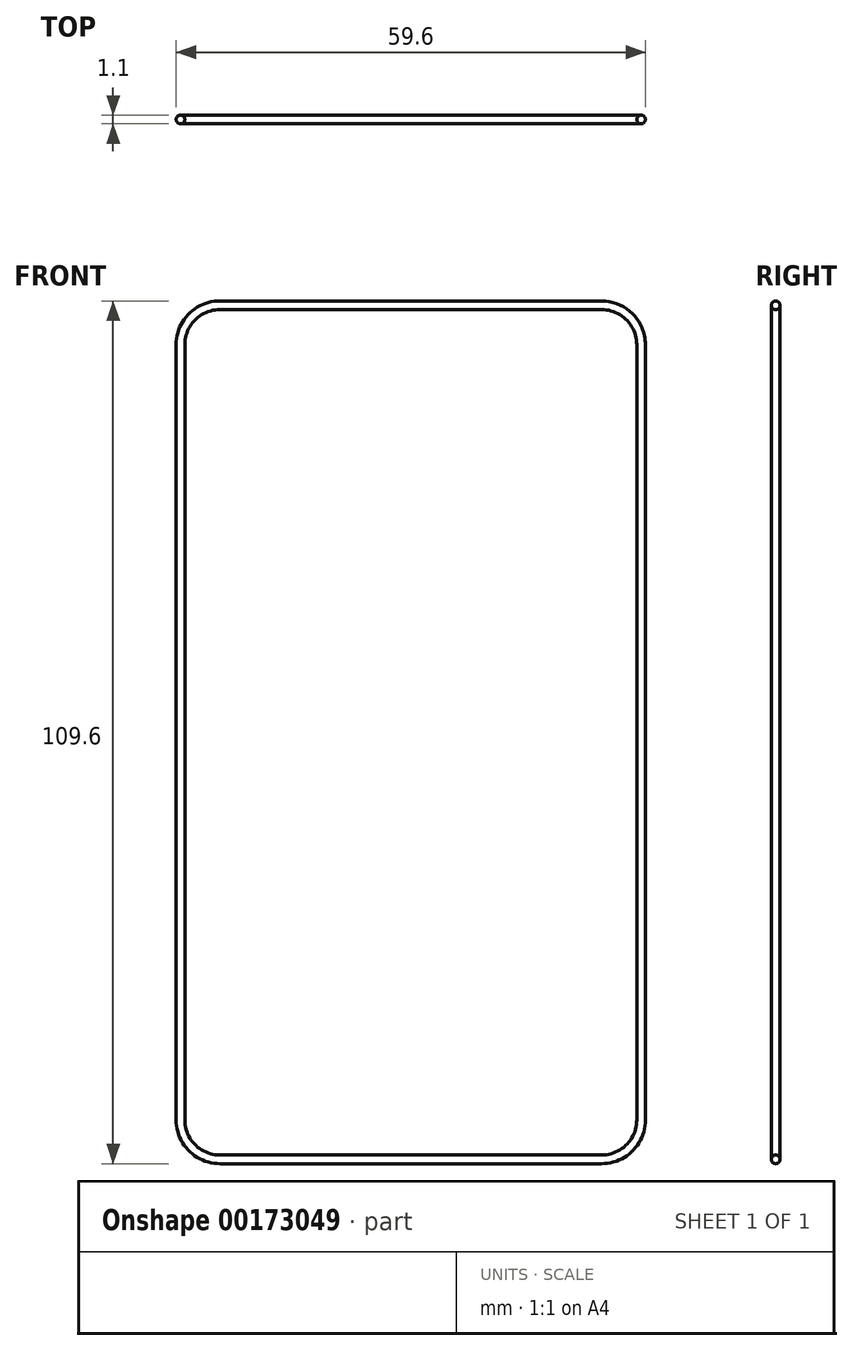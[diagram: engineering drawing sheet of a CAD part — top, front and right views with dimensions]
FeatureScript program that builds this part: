
annotation { "Feature Type Name" : "Feature", "Feature Type Description" : "" }
export const myFeature = defineFeature(function(context is Context, id is Id, definition is map)
    precondition{}
    {
        {
            var Q0;
            Q0=qCreatedBy(makeId("Front.planeOp"),FACE);
            var sketch = newSketch(context, id + "F0", { "sketchPlane" : qUnion([Q0])});
            skLineSegment(sketch, "E0.bottom", {"start": v(-24.25, 54.25) * mm, "end": v(24.25, 54.25) * mm});
            skLineSegment(sketch, "E0.top", {"start": v(-24.25, -54.25) * mm, "end": v(24.25, -54.25) * mm});
            skLineSegment(sketch, "E0.left", {"start": v(-29.25, 49.25) * mm, "end": v(-29.25, -49.25) * mm});
            skLineSegment(sketch, "E0.right", {"start": v(29.25, 49.25) * mm, "end": v(29.25, -49.25) * mm});
            skPoint(sketch, "E1.visualSharp", {"position": v(-29.25, 54.25) * mm});
            skArc(sketch, "E1.filletArc", {"start": v(-24.25, 54.25) * mm, "mid": v(-27.79, 52.79) * mm, "end": v(-29.25, 49.25) * mm});
            skPoint(sketch, "E2.visualSharp", {"position": v(29.25, 54.25) * mm});
            skArc(sketch, "E2.filletArc", {"start": v(29.25, 49.25) * mm, "mid": v(27.79, 52.79) * mm, "end": v(24.25, 54.25) * mm});
            skPoint(sketch, "E3.visualSharp", {"position": v(29.25, -54.25) * mm});
            skArc(sketch, "E3.filletArc", {"start": v(24.25, -54.25) * mm, "mid": v(27.79, -52.79) * mm, "end": v(29.25, -49.25) * mm});
            skPoint(sketch, "E4.visualSharp", {"position": v(-29.25, -54.25) * mm});
            skArc(sketch, "E4.filletArc", {"start": v(-29.25, -49.25) * mm, "mid": v(-27.79, -52.79) * mm, "end": v(-24.25, -54.25) * mm});
            skSolve(sketch);
        }
        {
            var Q0;
            Q0=sQuery(id+"F0.wireOp",VERTEX,"E1.filletArc.start");
            var Q1;
            Q1=qCreatedBy(makeId("Right.planeOp"),FACE);
            cPlane(context, id + "F1", {"entities" : qUnion([Q0, Q1]), "cplaneType" : CPlaneType.PLANE_POINT, "offset" : 25 * mm, "width" : 150 * mm, "height" : 150 * mm});
        }
        {
            var Q0;
            Q0=qCreatedBy(id+"F1.planeOp",FACE);
            var sketch = newSketch(context, id + "F2", { "sketchPlane" : qUnion([Q0])});
            skCircle(sketch, "E5", {"center": v(0, 54.25) * mm, "radius": 0.55 * mm});
            skSolve(sketch);
        }
        {
            var Q0;
            Q0=qSketchRegion(id+"F2",true);
            var Q1;
            Q1=sQuery(id+"F0.wireOp",EDGE,"E0.bottom");
            var Q2;
            Q2=sQuery(id+"F0.wireOp",EDGE,"E2.filletArc");
            var Q3;
            Q3=sQuery(id+"F0.wireOp",EDGE,"E0.right");
            var Q4;
            Q4=sQuery(id+"F0.wireOp",EDGE,"E3.filletArc");
            var Q5;
            Q5=sQuery(id+"F0.wireOp",EDGE,"E0.top");
            var Q6;
            Q6=sQuery(id+"F0.wireOp",EDGE,"E4.filletArc");
            var Q7;
            Q7=sQuery(id+"F0.wireOp",EDGE,"E0.left");
            var Q8;
            Q8=sQuery(id+"F0.wireOp",EDGE,"E1.filletArc");
            sweep(context, id + "F3", {"profiles" : qUnion([Q0]), "path" : qUnion([Q1, Q2, Q3, Q4, Q5, Q6, Q7, Q8])});
        }
    });
